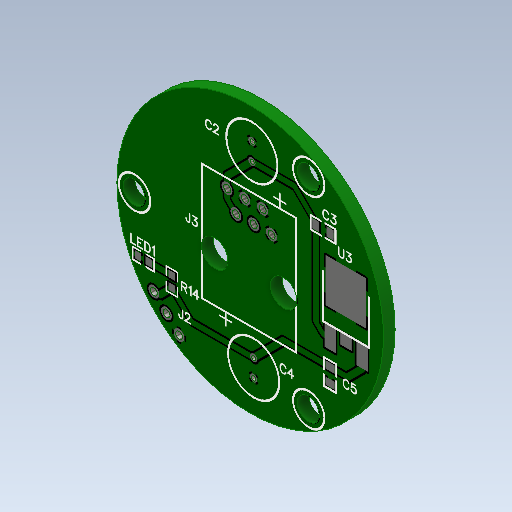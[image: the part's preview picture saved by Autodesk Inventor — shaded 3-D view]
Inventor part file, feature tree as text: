
AUTODESK INVENTOR PART (.ipt)
format: ipt  version: 2020 (Build 240168000, 168)  size: 241,152 bytes
history: native  units: in
note: dims shown in document units (in); Inventor stores cm internally (conversion verified against a paired STEP export)
features: other x4, sketch x4, projected_geometry x3, extrude x2
ambient origin geometry x8: Origin, YZ Plane, XZ Plane, XY Plane, X Axis, Y Axis, Z Axis, Center Point
bodies: Solid1 (feature_tree)
feature tree (13):
  extrude  "Extrusion1"  Depth=0.065in TaperAngle=0.0deg
  other  "Decal1"
  other  "Decal2"
  extrude  "Extrusion2"  Depth=0.1in
  sketch  "Sketch1"  dims[d0=1.5in d1=0.065in d2=0.0in]
  sketch  "Sketch2"  dims[d8=0.125in d9=0.1in]
  projected_geometry  "Projected Loop1"
  sketch  "Sketch3"  dims[d10=0.1in]
  projected_geometry  "Projected Loop2"
  sketch  "Sketch4"  dims[d11=0.1in d12=0.05in d13=0.1in d14=0.1in d15=0.04in d16=0.47in d17=0.62in d18=0.025in d19=0.025in d20=0.17in d21=0.099in d22=0.761in d23=0.04in d26=0.2in d27=45.0deg d28=0.18in d29=0.35in d30=0.025in d31=0.025in d32=0.099in d33=0.18in d34=0.77in d35=0.388in d36=0.15in d37=0.55in d38=0.82in d39=0.0in d40=0.0in d41=0.98in d42=0.1842in d43=1.3158in d44=1.0767in]
  projected_geometry  "Projected Loop3"
  other  "Image3"
  other  "Image4"
